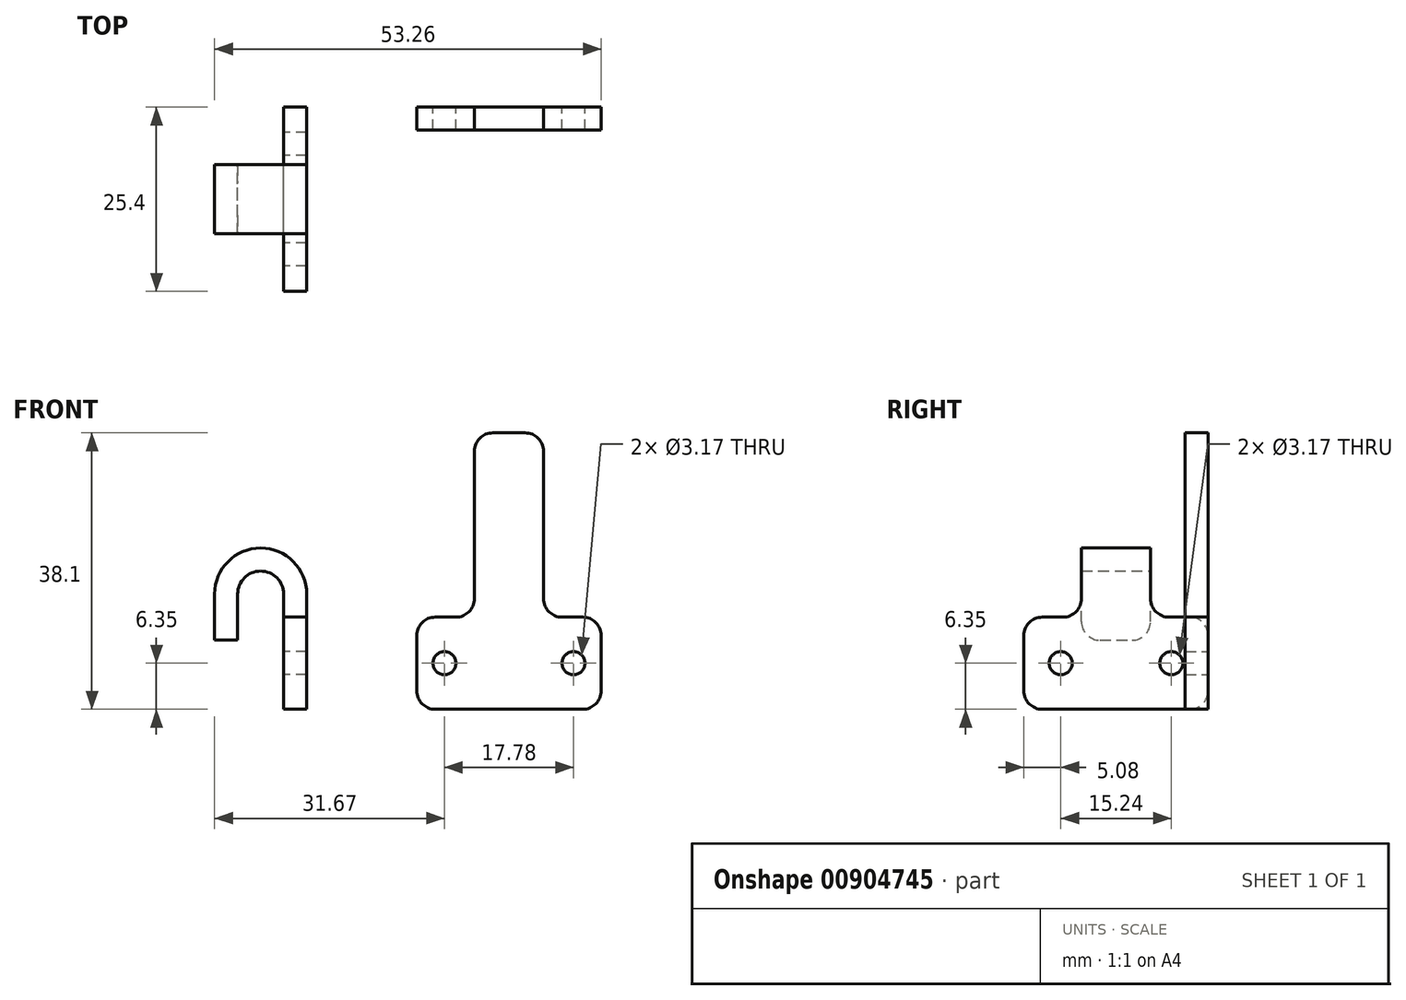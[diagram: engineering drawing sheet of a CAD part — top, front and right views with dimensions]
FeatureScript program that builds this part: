
annotation { "Feature Type Name" : "Feature", "Feature Type Description" : "" }
export const myFeature = defineFeature(function(context is Context, id is Id, definition is map)
    precondition{}
    {
        {
            var Q0;
            Q0=qCreatedBy(makeId("Front.planeOp"),FACE);
            var sketch = newSketch(context, id + "F0", { "sketchPlane" : qUnion([Q0])});
            skLineSegment(sketch, "E0.bottom", {"start": v(10.16, -6.35) * mm, "end": v(-10.16, -6.35) * mm});
            skLineSegment(sketch, "E0.top", {"start": v(10.16, 6.35) * mm, "end": v(7.3, 6.35) * mm});
            skLineSegment(sketch, "E0.left", {"start": v(12.7, -3.8) * mm, "end": v(12.7, 3.81) * mm});
            skLineSegment(sketch, "E0.right", {"start": v(-12.7, -3.8) * mm, "end": v(-12.7, 3.8) * mm});
            skPoint(sketch, "E0.middle", {"position": v(0, 0) * mm});
            skLineSegment(sketch, "E1.bottom", {"start": v(2.22, 31.75) * mm, "end": v(-2.22, 31.75) * mm});
            skLineSegment(sketch, "E1.left", {"start": v(4.76, 29.21) * mm, "end": v(4.76, 8.9) * mm});
            skLineSegment(sketch, "E1.right", {"start": v(-4.76, 29.21) * mm, "end": v(-4.76, 8.9) * mm});
            skPoint(sketch, "E1.middle", {"position": v(0, 6.35) * mm});
            skPoint(sketch, "E1.top.end.orphan", {"position": v(-4.76, -19.05) * mm});
            skPoint(sketch, "E1.top.start.orphan", {"position": v(4.76, -19.05) * mm});
            skLineSegment(sketch, "E2.trimOffspring", {"start": v(-7.3, 6.35) * mm, "end": v(-10.16, 6.35) * mm});
            skPoint(sketch, "E3.visualSharp", {"position": v(-12.7, 6.35) * mm});
            skArc(sketch, "E3.filletArc", {"start": v(-10.16, 6.35) * mm, "mid": v(-11.96, 5.6) * mm, "end": v(-12.7, 3.81) * mm});
            skPoint(sketch, "E4.visualSharp", {"position": v(-12.7, -6.35) * mm});
            skArc(sketch, "E4.filletArc", {"start": v(-12.7, -3.8) * mm, "mid": v(-11.96, -5.6) * mm, "end": v(-10.16, -6.35) * mm});
            skPoint(sketch, "E5.visualSharp", {"position": v(12.7, -6.35) * mm});
            skArc(sketch, "E5.filletArc", {"start": v(10.16, -6.35) * mm, "mid": v(11.96, -5.6) * mm, "end": v(12.7, -3.8) * mm});
            skPoint(sketch, "E6.visualSharp", {"position": v(12.7, 6.35) * mm});
            skArc(sketch, "E6.filletArc", {"start": v(12.7, 3.81) * mm, "mid": v(11.96, 5.6) * mm, "end": v(10.16, 6.35) * mm});
            skCircle(sketch, "E7", {"center": v(-8.9, 0) * mm, "radius": 1.59 * mm});
            skCircle(sketch, "E8.MirrorC", {"center": v(8.9, 0) * mm, "radius": 1.59 * mm});
            skPoint(sketch, "E9.visualSharp", {"position": v(-4.76, 6.35) * mm});
            skArc(sketch, "E9.filletArc", {"start": v(-7.3, 6.35) * mm, "mid": v(-5.5, 7.1) * mm, "end": v(-4.76, 8.9) * mm});
            skPoint(sketch, "E10.visualSharp", {"position": v(4.76, 6.35) * mm});
            skArc(sketch, "E10.filletArc", {"start": v(4.76, 8.9) * mm, "mid": v(5.5, 7.1) * mm, "end": v(7.3, 6.35) * mm});
            skPoint(sketch, "E11.visualSharp", {"position": v(4.76, 31.75) * mm});
            skArc(sketch, "E11.filletArc", {"start": v(4.76, 29.21) * mm, "mid": v(4.02, 31) * mm, "end": v(2.22, 31.75) * mm});
            skPoint(sketch, "E12.visualSharp", {"position": v(-4.76, 31.75) * mm});
            skArc(sketch, "E12.filletArc", {"start": v(-2.22, 31.75) * mm, "mid": v(-4.02, 31) * mm, "end": v(-4.76, 29.21) * mm});
            skSolve(sketch);
        }
        {
            var Q0;
            Q0=makeQuery(id+"F0.imprint","IMPRINT",FACE,{"disambiguationData":[TD([[makeQuery(id+"F0.imprint","IMPRINT",EDGE,{"derivedFrom":sQuery(id+"F0.wireOp",EDGE,"E0.bottom")}),-1.0]])]});
            extrude(context, id + "F1", {"entities" : qUnion([Q0]), "depth" : 3.17 * mm, "offsetDistance" : 25.4 * mm});
        }
        {
            var Q0;
            Q0=qCreatedBy(makeId("Front.planeOp"),FACE);
            var sketch = newSketch(context, id + "F2", { "sketchPlane" : qUnion([Q0])});
            skLineSegment(sketch, "E13.bottom", {"start": v(-27.86, -6.35) * mm, "end": v(-31.04, -6.35) * mm});
            skLineSegment(sketch, "E13.left", {"start": v(-27.86, -6.35) * mm, "end": v(-27.86, 6.35) * mm});
            skLineSegment(sketch, "E13.right", {"start": v(-31.04, -6.35) * mm, "end": v(-31.04, 6.35) * mm});
            skPoint(sketch, "E13.middle", {"position": v(-29.45, 0) * mm});
            skLineSegment(sketch, "E14.left", {"start": v(-27.86, 6.35) * mm, "end": v(-27.86, 9.53) * mm});
            skLineSegment(sketch, "E14.right", {"start": v(-31.04, 6.35) * mm, "end": v(-31.04, 9.53) * mm});
            skLineSegment(sketch, "E15", {"start": v(-34.21, 12.31) * mm, "end": v(-34.21, 6.74) * mm, "construction": true});
            skArc(sketch, "E16", {"start": v(-31.04, 9.53) * mm, "mid": v(-34.21, 12.7) * mm, "end": v(-37.39, 9.53) * mm});
            skLineSegment(sketch, "E17.bottom", {"start": v(-37.39, 3.18) * mm, "end": v(-40.56, 3.17) * mm});
            skLineSegment(sketch, "E17.left", {"start": v(-37.39, 3.18) * mm, "end": v(-37.39, 9.53) * mm});
            skLineSegment(sketch, "E17.right", {"start": v(-40.56, 3.18) * mm, "end": v(-40.56, 9.52) * mm});
            skArc(sketch, "E18.trimOffspring", {"start": v(-27.86, 9.53) * mm, "mid": v(-34.21, 15.88) * mm, "end": v(-40.56, 9.52) * mm});
            skSolve(sketch);
        }
        {
            var Q0;
            Q0=makeQuery(id+"F2.imprint","IMPRINT",FACE,{"disambiguationData":[TD([[makeQuery(id+"F2.imprint","IMPRINT",EDGE,{"derivedFrom":sQuery(id+"F2.wireOp",EDGE,"E13.bottom")}),-1.0]])]});
            extrude(context, id + "F3", {"entities" : qUnion([Q0]), "depth" : 25.4 * mm, "offsetDistance" : 25.4 * mm});
        }
        {
            var Q0;
            Q0=makeQuery(id+"F3.opExtrude","SWEPT_FACE",FACE,{"disambiguationData":[OSD([sQuery(id+"F2.wireOp",EDGE,"E13.right"),sQuery(id+"F2.wireOp",EDGE,"E14.right")])]});
            var sketch = newSketch(context, id + "F4", { "sketchPlane" : qUnion([Q0])});
            skLineSegment(sketch, "E19.bottom", {"start": v(2.54, -6.35) * mm, "end": v(22.86, -6.35) * mm});
            skLineSegment(sketch, "E19.top", {"start": v(2.54, 6.35) * mm, "end": v(7.94, 6.35) * mm});
            skLineSegment(sketch, "E19.left", {"start": v(0, -3.8) * mm, "end": v(0, 3.81) * mm});
            skLineSegment(sketch, "E19.right", {"start": v(25.4, -3.8) * mm, "end": v(25.4, 3.81) * mm});
            skLineSegment(sketch, "E20.bottom", {"start": v(17.46, 19.05) * mm, "end": v(7.94, 19.05) * mm});
            skLineSegment(sketch, "E20.top", {"start": v(17.46, -6.35) * mm, "end": v(7.94, -6.35) * mm});
            skLineSegment(sketch, "E20.left", {"start": v(17.46, 19.05) * mm, "end": v(17.46, 6.35) * mm});
            skLineSegment(sketch, "E20.right", {"start": v(7.94, 19.05) * mm, "end": v(7.94, 6.35) * mm});
            skPoint(sketch, "E20.middle", {"position": v(12.7, 6.35) * mm});
            skLineSegment(sketch, "E21.trimOffspring", {"start": v(17.46, 6.35) * mm, "end": v(22.86, 6.35) * mm});
            skPoint(sketch, "E22.visualSharp", {"position": v(0, 6.35) * mm});
            skArc(sketch, "E22.filletArc", {"start": v(2.54, 6.35) * mm, "mid": v(0.74, 5.6) * mm, "end": v(0, 3.81) * mm});
            skPoint(sketch, "E23.visualSharp", {"position": v(0, -6.35) * mm});
            skArc(sketch, "E23.filletArc", {"start": v(0, -3.8) * mm, "mid": v(0.74, -5.6) * mm, "end": v(2.54, -6.35) * mm});
            skPoint(sketch, "E24.visualSharp", {"position": v(25.4, -6.35) * mm});
            skArc(sketch, "E24.filletArc", {"start": v(22.86, -6.35) * mm, "mid": v(24.66, -5.6) * mm, "end": v(25.4, -3.8) * mm});
            skPoint(sketch, "E25.visualSharp", {"position": v(25.4, 6.35) * mm});
            skArc(sketch, "E25.filletArc", {"start": v(25.4, 3.81) * mm, "mid": v(24.66, 5.6) * mm, "end": v(22.86, 6.35) * mm});
            skLineSegment(sketch, "E26.bottom", {"start": v(45.34, -23.04) * mm, "end": v(-19.94, -23.04) * mm});
            skLineSegment(sketch, "E26.top", {"start": v(45.34, 35.74) * mm, "end": v(-19.94, 35.74) * mm});
            skLineSegment(sketch, "E26.left", {"start": v(45.34, -23.04) * mm, "end": v(45.34, 35.74) * mm});
            skLineSegment(sketch, "E26.right", {"start": v(-19.94, -23.04) * mm, "end": v(-19.94, 35.74) * mm});
            skSolve(sketch);
        }
        {
            var Q0;
            {var subQ18=sQuery(id+"F4.wireOp",EDGE,"E19.left");Q0=makeQuery(id+"F4.imprint","IMPRINT",FACE,{"disambiguationData":[TD([[makeQuery(id+"F4.imprint","IMPRINT",EDGE,{"derivedFrom":subQ18}),1.0]])]});}
            var Q1;
            {var subQ1=sQuery(id+"F4.wireOp",EDGE,"E19.top");Q1=makeQuery(id+"F4.imprint","IMPRINT",FACE,{"disambiguationData":[TD([[makeQuery(id+"F4.imprint","IMPRINT",EDGE,{"derivedFrom":subQ1}),1.0]])]});}
            var Q2;
            {var subQ1=sQuery(id+"F4.wireOp",EDGE,"E21.trimOffspring");Q2=makeQuery(id+"F4.imprint","IMPRINT",FACE,{"disambiguationData":[TD([[makeQuery(id+"F4.imprint","IMPRINT",EDGE,{"derivedFrom":subQ1}),1.0]])]});}
            extrude(context, id + "F5", {"entities" : qUnion([Q0, Q1, Q2]), "operationType" : NewBodyOperationType.REMOVE, "endBound" : BoundingType.SYMMETRIC, "depth" : 25.4 * mm, "offsetDistance" : 25.4 * mm});
        }
        {
            var Q0;
            Q0=makeQuery(id+"F3.opExtrude","SWEPT_FACE",FACE,{"disambiguationData":[OSD([sQuery(id+"F2.wireOp",EDGE,"E17.right")])]});
            var sketch = newSketch(context, id + "F6", { "sketchPlane" : qUnion([Q0])});
            skLineSegment(sketch, "E27.bottom", {"start": v(14.92, 3.18) * mm, "end": v(10.48, 3.18) * mm});
            skLineSegment(sketch, "E27.top", {"start": v(17.46, 15.88) * mm, "end": v(7.94, 15.88) * mm});
            skLineSegment(sketch, "E27.left", {"start": v(17.46, 5.72) * mm, "end": v(17.46, 15.88) * mm});
            skLineSegment(sketch, "E27.right", {"start": v(7.94, 5.72) * mm, "end": v(7.94, 15.88) * mm});
            skPoint(sketch, "E27.middle", {"position": v(12.7, 9.53) * mm});
            skPoint(sketch, "E28.visualSharp", {"position": v(7.94, 3.18) * mm});
            skArc(sketch, "E28.filletArc", {"start": v(7.94, 5.72) * mm, "mid": v(8.68, 3.92) * mm, "end": v(10.48, 3.18) * mm});
            skPoint(sketch, "E29.visualSharp", {"position": v(17.46, 3.18) * mm});
            skArc(sketch, "E29.filletArc", {"start": v(14.92, 3.18) * mm, "mid": v(16.72, 3.92) * mm, "end": v(17.46, 5.72) * mm});
            skLineSegment(sketch, "E30.bottom", {"start": v(27.72, -2.32) * mm, "end": v(-2.32, -2.32) * mm});
            skLineSegment(sketch, "E30.top", {"start": v(27.72, 21.37) * mm, "end": v(-2.32, 21.37) * mm});
            skLineSegment(sketch, "E30.left", {"start": v(27.72, -2.32) * mm, "end": v(27.72, 21.37) * mm});
            skLineSegment(sketch, "E30.right", {"start": v(-2.32, -2.32) * mm, "end": v(-2.32, 21.37) * mm});
            skSolve(sketch);
        }
        {
            var Q0;
            {var subQ4=sQuery(id+"F6.wireOp",EDGE,"E28.filletArc");Q0=makeQuery(id+"F6.imprint","IMPRINT",FACE,{"disambiguationData":[TD([[makeQuery(id+"F6.imprint","IMPRINT",EDGE,{"derivedFrom":subQ4}),-1.0]])]});}
            var Q1;
            {var subQ2=sQuery(id+"F6.wireOp",EDGE,"E29.filletArc");Q1=makeQuery(id+"F6.imprint","IMPRINT",FACE,{"disambiguationData":[TD([[makeQuery(id+"F6.imprint","IMPRINT",EDGE,{"derivedFrom":subQ2}),-1.0]])]});}
            extrude(context, id + "F7", {"entities" : qUnion([Q0, Q1]), "operationType" : NewBodyOperationType.REMOVE, "oppositeDirection" : true, "depth" : 6.35 * mm, "offsetDistance" : 25.4 * mm});
        }
        {
            var Q0;
            {var subQ0=sQuery(id+"F4.wireOp",EDGE,"E19.top");var subQ1=sQuery(id+"F4.wireOp",EDGE,"E20.right");Q0=makeQuery(id+"F5.boolean.opBoolean","COPY",EDGE,{"disambiguationData":[TD([makeQuery(id+"F3.opExtrude","SWEPT_FACE",FACE,{"disambiguationData":[OSD([sQuery(id+"F2.wireOp",EDGE,"E13.left"),sQuery(id+"F2.wireOp",EDGE,"E14.left")])]})])],"derivedFrom":makeQuery(id+"F5.opExtrude","SWEPT_EDGE",EDGE,{"disambiguationData":[OSD([subQ0,subQ1])]})});}
            var Q1;
            {var subQ0=sQuery(id+"F4.wireOp",EDGE,"E20.left");var subQ1=sQuery(id+"F4.wireOp",EDGE,"E21.trimOffspring");Q1=makeQuery(id+"F5.boolean.opBoolean","COPY",EDGE,{"disambiguationData":[TD([makeQuery(id+"F3.opExtrude","SWEPT_FACE",FACE,{"disambiguationData":[OSD([sQuery(id+"F2.wireOp",EDGE,"E13.left"),sQuery(id+"F2.wireOp",EDGE,"E14.left")])]})])],"derivedFrom":makeQuery(id+"F5.opExtrude","SWEPT_EDGE",EDGE,{"disambiguationData":[OSD([subQ0,subQ1])]})});}
            var Q2;
            Q2=makeQuery(id+"F3.opExtrude","CAP_EDGE",EDGE,{"disambiguationData":[OSD([sQuery(id+"F2.wireOp",EDGE,"E13.bottom")])],"isStart":false});
            var Q3;
            Q3=makeQuery(id+"F3.opExtrude","CAP_EDGE",EDGE,{"disambiguationData":[OSD([sQuery(id+"F2.wireOp",EDGE,"E13.bottom")])],"isStart":true});
            fillet(context, id + "F8", {"entities" : qUnion([Q0, Q1, Q2, Q3]), "radius" : 2.54 * mm, "tangentPropagation" : true, "allowEdgeOverflow" : false});
        }
        {
            var Q0;
            Q0=makeQuery(id+"F3.opExtrude","SWEPT_FACE",FACE,{"disambiguationData":[OSD([sQuery(id+"F2.wireOp",EDGE,"E13.right"),sQuery(id+"F2.wireOp",EDGE,"E14.right")])]});
            var sketch = newSketch(context, id + "F9", { "sketchPlane" : qUnion([Q0])});
            skLineSegment(sketch, "E31", {"start": v(0, 0) * mm, "end": v(25.4, 0) * mm, "construction": true});
            skCircle(sketch, "E32", {"center": v(5.08, 0) * mm, "radius": 1.59 * mm});
            skCircle(sketch, "E33", {"center": v(20.32, 0) * mm, "radius": 1.59 * mm});
            skSolve(sketch);
        }
        {
            var Q0;
            Q0 = qSketchRegion(id + "F9", true);
            extrude(context, id + "F10", {"entities" : qUnion([Q0]), "operationType" : NewBodyOperationType.REMOVE, "oppositeDirection" : true, "depth" : 25.4 * mm, "offsetDistance" : 25.4 * mm});
        }
    });
